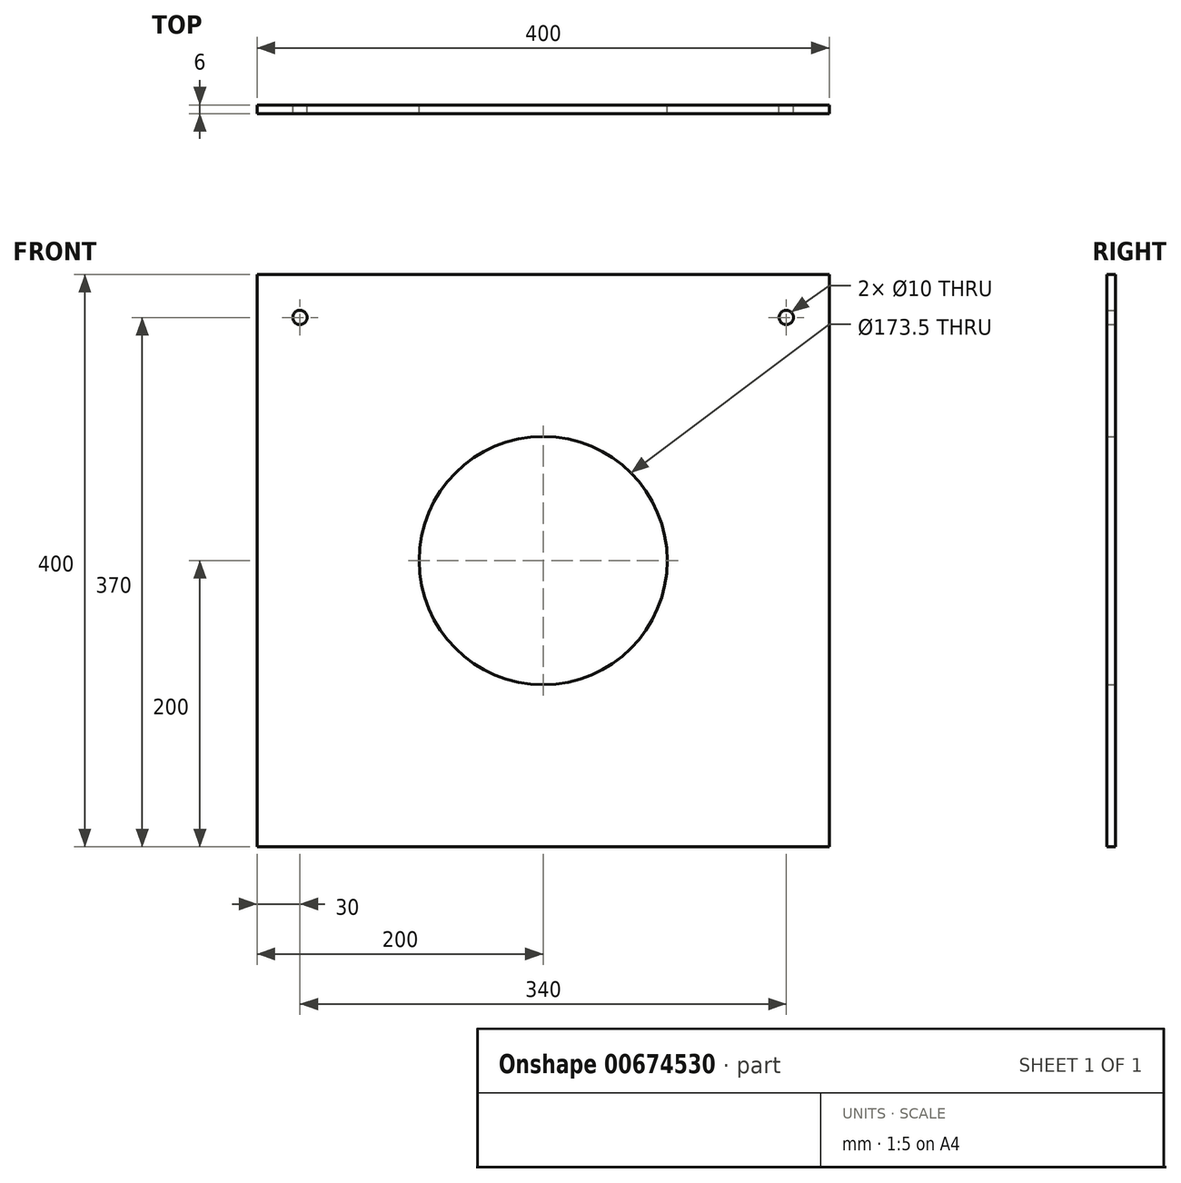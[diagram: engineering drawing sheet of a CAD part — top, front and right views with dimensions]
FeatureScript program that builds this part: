
annotation { "Feature Type Name" : "Feature", "Feature Type Description" : "" }
export const myFeature = defineFeature(function(context is Context, id is Id, definition is map)
    precondition{}
    {
        {
            var Q0;
            Q0=qCreatedBy(makeId("Front.planeOp"),FACE);
            var sketch = newSketch(context, id + "F0", { "sketchPlane" : qUnion([Q0])});
            skLineSegment(sketch, "E0.bottom", {"start": v(-200, 200) * mm, "end": v(200, 200) * mm});
            skLineSegment(sketch, "E0.top", {"start": v(-200, -200) * mm, "end": v(200, -200) * mm});
            skLineSegment(sketch, "E0.left", {"start": v(-200, 200) * mm, "end": v(-200, -200) * mm});
            skLineSegment(sketch, "E0.right", {"start": v(200, 200) * mm, "end": v(200, -200) * mm});
            skPoint(sketch, "E0.middle", {"position": v(0, 0) * mm});
            skCircle(sketch, "E1", {"center": v(170, 170) * mm, "radius": 5 * mm});
            skCircle(sketch, "E2", {"center": v(-170, 170) * mm, "radius": 5 * mm});
            skCircle(sketch, "E3", {"center": v(0, 0) * mm, "radius": 86.75 * mm});
            skSolve(sketch);
        }
        {
            var Q0;
            Q0 = qSketchRegion(id + "F0", true);
            extrude(context, id + "F1", {"entities" : qUnion([Q0]), "endBound" : BoundingType.SYMMETRIC, "depth" : 2 * mm, "offsetDistance" : 25 * mm});
        }
        {
            var Q0;
            Q0 = qSketchRegion(id + "F0", true);
            extrude(context, id + "F2", {"entities" : qUnion([Q0]), "operationType" : NewBodyOperationType.ADD, "depth" : 5 * mm, "offsetDistance" : 25 * mm});
        }
    });
